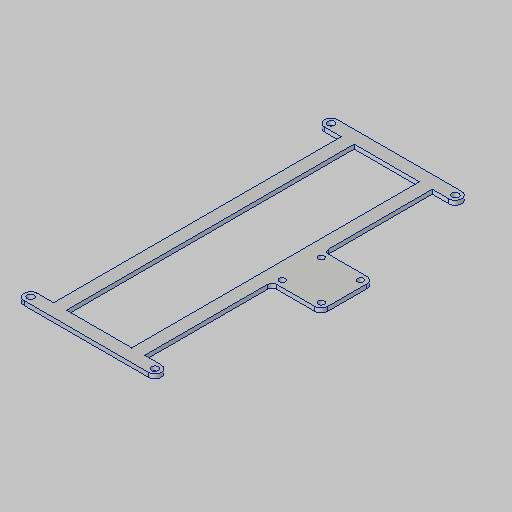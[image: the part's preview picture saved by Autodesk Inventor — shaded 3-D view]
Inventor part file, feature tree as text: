
AUTODESK INVENTOR PART (.ipt)
format: ipt  version: 2023.5 (Build 275446000, 446)  size: 192,512 bytes
history: native  units: in
note: dims shown in document units (in); Inventor stores cm internally (conversion verified against a paired STEP export)
features: sketch x3, extrude x2, hole x2, projected_geometry x2, fillet x1
ambient origin geometry x8: Origin, YZ Plane, XZ Plane, XY Plane, X Axis, Y Axis, Z Axis, Center Point
bodies: Solid1 (feature_tree)
feature tree (10):
  sketch  "Sketch1"  dims[d0=0.375in d1=3.62in]
  extrude  "Extrusion1"  Depth=0.375in
  sketch  "Sketch2"  dims[d2=8.75in d4=0.375in]
  hole  "Hole1"  [1 undecoded]
  sketch  "Sketch3"  dims[d5=1.9in d6=0.375in d7=0.375in d16=0.125in d17=0.0in d18=0.201in d19=0.75in d20=0.385in d21=0.25in d22=0.5635in d23=1.0in d24=0.8108in d33=1.14in d34=1.14in d35=0.375in d36=0.375in d37=0.625in d38=0.625in d39=0.625in d40=0.625in d48=1.245in d50=1.14in d51=0.375in d55=0.125in d56=0.0in d57=0.13in d58=0.177in d59=0.276in d60=0.332in d61=0.25in d62=0.5635in d63=1.0in d64=0.8108in d66=0.28in d67=1.14in]
  extrude  "Extrusion2"  Depth=0.375in
  fillet  "Fillet2"  Radius=0.375in
  hole  "Hole4"  [1 undecoded]
  projected_geometry  "Projected Loop1"
  projected_geometry  "Project Cut Edges1"
note: 2 required parameter values undecoded (feature->parameter linkage not recoverable at this tier; creation-order binding heuristic only, values carry confidence <= 0.55)
